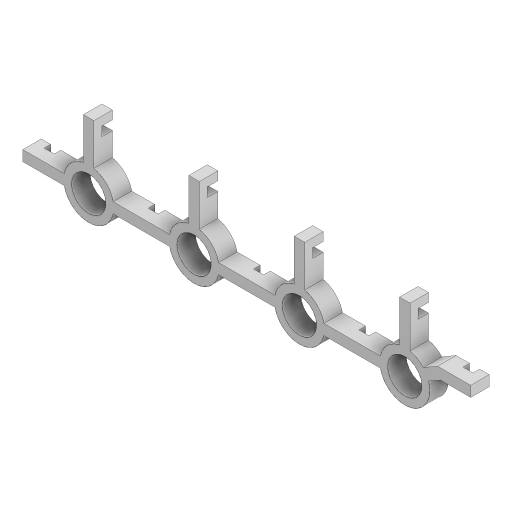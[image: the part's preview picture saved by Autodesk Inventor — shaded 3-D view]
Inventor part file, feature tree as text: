
AUTODESK INVENTOR PART (.ipt)
format: ipt  version: 2024 (Build 280153000, 153)  size: 293,888 bytes
history: native  units: in
note: dims shown in document units (in); Inventor stores cm internally (conversion verified against a paired STEP export)
features: extrude x6, sketch x6, other x1
ambient origin geometry x8: Origin, YZ Plane, XZ Plane, XY Plane, X Axis, Y Axis, Z Axis, Center Point
bodies: Body1 (feature_tree)
feature tree (13):
  other  "實體1"
  extrude  "擠出1"  Depth=0.5118in
  extrude  "擠出3"  Depth=0.748in
  extrude  "擠出4"  Depth=0.2756in TaperAngle=0.0deg
  extrude  "擠出5"  Depth=1.5748in
  extrude  "擠出6"  Depth=0.1575in
  extrude  "擠出7"  Depth=0.0787in
  sketch  "草圖1"
  sketch  "草圖3"
  sketch  "草圖4"
  sketch  "草圖5"
  sketch  "草圖6"
  sketch  "草圖7"
